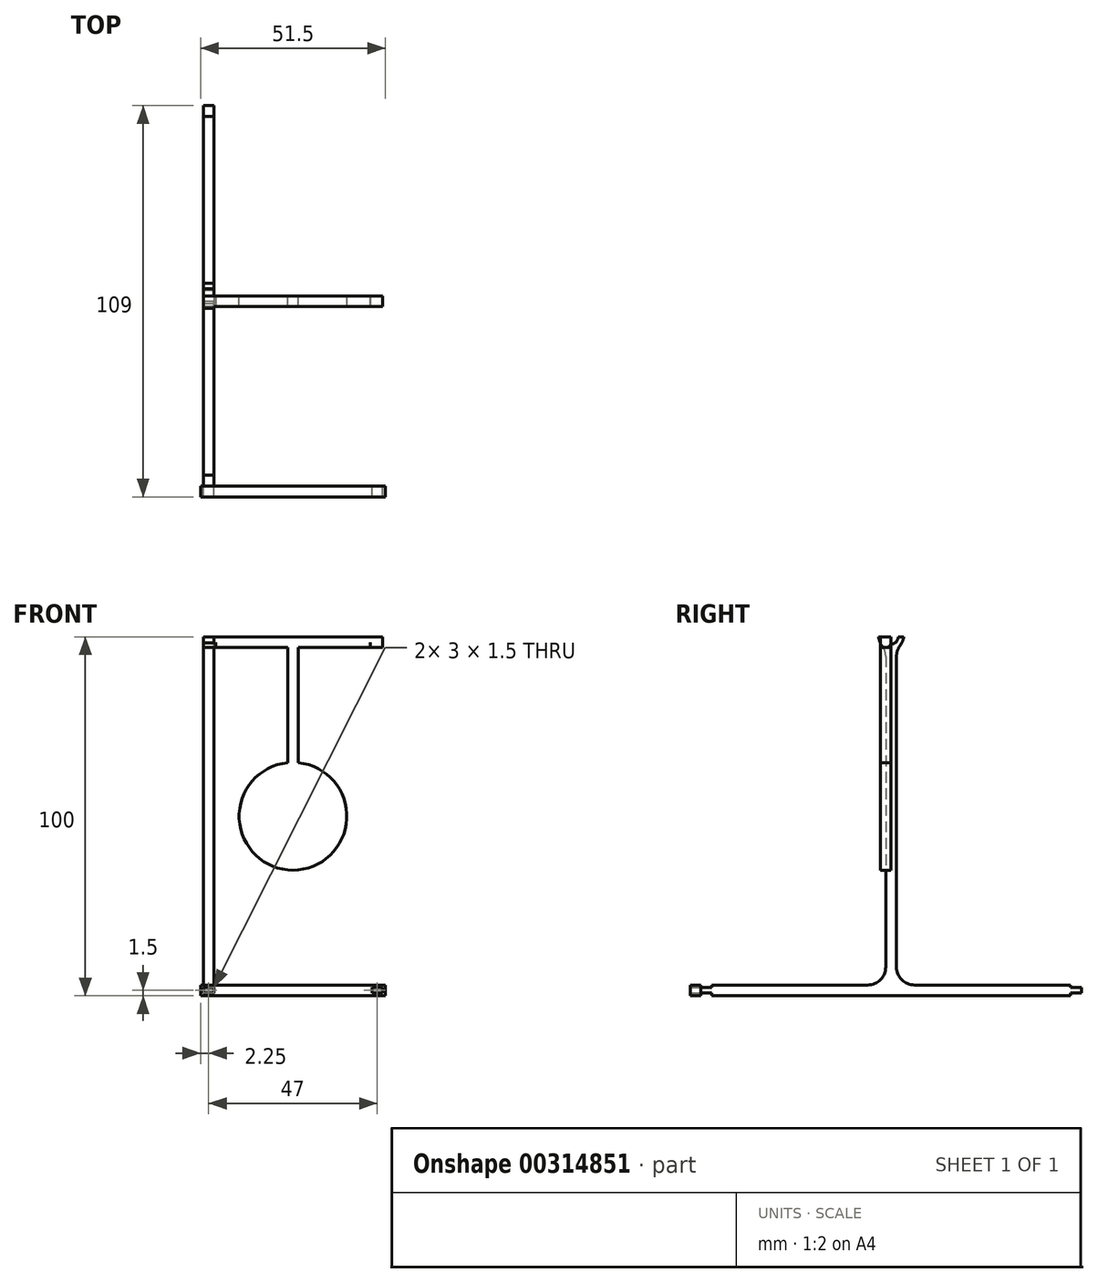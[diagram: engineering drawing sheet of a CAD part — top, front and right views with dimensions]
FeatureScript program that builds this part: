
annotation { "Feature Type Name" : "Feature", "Feature Type Description" : "" }
export const myFeature = defineFeature(function(context is Context, id is Id, definition is map)
    precondition{}
    {
        {
            var Q0;
            Q0=qCreatedBy(makeId("Right.planeOp"),FACE);
            var sketch = newSketch(context, id + "F0", { "sketchPlane" : qUnion([Q0])});
            skLineSegment(sketch, "E0", {"start": v(-2, 100) * mm, "end": v(-3.5, 100) * mm});
            skLineSegment(sketch, "E1", {"start": v(-3.5, 100) * mm, "end": v(-3.5, 98.5) * mm});
            skLineSegment(sketch, "E2", {"start": v(-50, 3) * mm, "end": v(-50, 2.25) * mm});
            skLineSegment(sketch, "E3", {"start": v(-50, 2.25) * mm, "end": v(-53, 2.25) * mm});
            skLineSegment(sketch, "E4", {"start": v(-53, 2.25) * mm, "end": v(-53, 0.75) * mm});
            skLineSegment(sketch, "E5", {"start": v(-53, 0.75) * mm, "end": v(-50, 0.75) * mm});
            skLineSegment(sketch, "E6", {"start": v(-50, 0.75) * mm, "end": v(-50, 0) * mm});
            skLineSegment(sketch, "E7", {"start": v(-50, 0) * mm, "end": v(0, 0) * mm});
            skArc(sketch, "E8", {"start": v(-2, 100) * mm, "mid": v(-1.41, 98.59) * mm, "end": v(0, 98) * mm});
            skPoint(sketch, "E8.third.point", {"position": v(0, 102) * mm});
            skPoint(sketch, "E9.start.orphan", {"position": v(0, 98) * mm});
            skLineSegment(sketch, "E10", {"start": v(-3.5, 98.5) * mm, "end": v(-1.5, 96.5) * mm});
            skLineSegment(sketch, "E11", {"start": v(-1.5, 96.5) * mm, "end": v(-1.5, 3) * mm});
            skLineSegment(sketch, "E12", {"start": v(-50, 3) * mm, "end": v(-1.5, 3) * mm});
            skLineSegment(sketch, "E13.MirrorCS", {"start": v(2, 100) * mm, "end": v(3.5, 100) * mm});
            skLineSegment(sketch, "E14.MirrorCS", {"start": v(3.5, 100) * mm, "end": v(3.5, 98.5) * mm});
            skLineSegment(sketch, "E15.MirrorCS", {"start": v(50, 3) * mm, "end": v(50, 2.25) * mm});
            skLineSegment(sketch, "E16.MirrorCS", {"start": v(50, 2.25) * mm, "end": v(53, 2.25) * mm});
            skLineSegment(sketch, "E17.MirrorCS", {"start": v(53, 2.25) * mm, "end": v(53, 0.75) * mm});
            skLineSegment(sketch, "E18.MirrorCS", {"start": v(53, 0.75) * mm, "end": v(50, 0.75) * mm});
            skLineSegment(sketch, "E19.MirrorCS", {"start": v(50, 0.75) * mm, "end": v(50, 0) * mm});
            skArc(sketch, "E20.MirrorCS", {"start": v(2, 100) * mm, "mid": v(1.41, 98.59) * mm, "end": v(0, 98) * mm});
            skLineSegment(sketch, "E21.MirrorCS", {"start": v(3.5, 98.5) * mm, "end": v(1.5, 96.5) * mm});
            skLineSegment(sketch, "E22.MirrorCS", {"start": v(50, 0) * mm, "end": v(0, 0) * mm});
            skLineSegment(sketch, "E23.MirrorCS", {"start": v(1.5, 96.5) * mm, "end": v(1.5, 3) * mm});
            skLineSegment(sketch, "E24.MirrorCS", {"start": v(50, 3) * mm, "end": v(1.5, 3) * mm});
            skSolve(sketch);
        }
        {
            var Q0;
            Q0=makeQuery(id+"F0.imprint","IMPRINT",FACE,{"disambiguationData":[TD([[makeQuery(id+"F0.imprint","IMPRINT",EDGE,{"derivedFrom":sQuery(id+"F0.wireOp",EDGE,"E0")}),1.0]])]});
            extrude(context, id + "F1", {"entities" : qUnion([Q0]), "depth" : 3 * mm});
        }
        {
            var Q0;
            Q0=makeQuery(id+"F1.opExtrude","SWEPT_EDGE",EDGE,{"disambiguationData":[OSD([sQuery(id+"F0.wireOp",EDGE,"E11"),sQuery(id+"F0.wireOp",EDGE,"E12")])]});
            var Q1;
            Q1=makeQuery(id+"F1.opExtrude","SWEPT_EDGE",EDGE,{"disambiguationData":[OSD([sQuery(id+"F0.wireOp",EDGE,"E23.MirrorCS"),sQuery(id+"F0.wireOp",EDGE,"E24.MirrorCS")])]});
            var Q2;
            Q2=makeQuery(id+"F1.opExtrude","SWEPT_EDGE",EDGE,{"disambiguationData":[OSD([sQuery(id+"F0.wireOp",EDGE,"E14.MirrorCS"),sQuery(id+"F0.wireOp",EDGE,"E21.MirrorCS")])]});
            var Q3;
            Q3=makeQuery(id+"F1.opExtrude","SWEPT_EDGE",EDGE,{"disambiguationData":[OSD([sQuery(id+"F0.wireOp",EDGE,"E1"),sQuery(id+"F0.wireOp",EDGE,"E10")])]});
            fillet(context, id + "F2", {"entities" : qUnion([Q0, Q1, Q2, Q3]), "radius" : 5 * mm, "tangentPropagation" : true, "allowEdgeOverflow" : false});
        }
        {
            var Q0;
            Q0=makeQuery(id+"F1.opExtrude","SWEPT_EDGE",EDGE,{"disambiguationData":[OSD([sQuery(id+"F0.wireOp",EDGE,"E10"),sQuery(id+"F0.wireOp",EDGE,"E11")])]});
            var Q1;
            Q1=makeQuery(id+"F1.opExtrude","SWEPT_EDGE",EDGE,{"disambiguationData":[OSD([sQuery(id+"F0.wireOp",EDGE,"E21.MirrorCS"),sQuery(id+"F0.wireOp",EDGE,"E23.MirrorCS")])]});
            fillet(context, id + "F3", {"entities" : qUnion([Q0, Q1]), "radius" : 5 * mm, "tangentPropagation" : true, "allowEdgeOverflow" : false});
        }
        {
            var Q0;
            Q0=makeQuery(id+"F1.opExtrude","SWEPT_FACE",FACE,{"disambiguationData":[OSD([sQuery(id+"F0.wireOp",EDGE,"E4")])]});
            var sketch = newSketch(context, id + "F4", { "sketchPlane" : qUnion([Q0])});
            skLineSegment(sketch, "E25.bottom", {"start": v(0, 2.25) * mm, "end": v(3, 2.25) * mm});
            skLineSegment(sketch, "E25.top", {"start": v(0, 0.75) * mm, "end": v(3, 0.75) * mm});
            skLineSegment(sketch, "E25.left", {"start": v(0, 2.25) * mm, "end": v(0, 0.75) * mm});
            skLineSegment(sketch, "E25.right", {"start": v(3, 2.25) * mm, "end": v(3, 0.75) * mm});
            skLineSegment(sketch, "E26", {"start": v(0, 0) * mm, "end": v(25, 0) * mm});
            skLineSegment(sketch, "E27.0.3", {"start": v(3, 3) * mm, "end": v(0, 3) * mm});
            skLineSegment(sketch, "E28", {"start": v(0, 3) * mm, "end": v(-0.75, 3) * mm});
            skLineSegment(sketch, "E29", {"start": v(-0.75, 3) * mm, "end": v(-0.75, 0) * mm});
            skLineSegment(sketch, "E30", {"start": v(-0.75, 0) * mm, "end": v(0, 0) * mm});
            skLineSegment(sketch, "E31", {"start": v(3, 3) * mm, "end": v(25, 3) * mm});
            skLineSegment(sketch, "E32", {"start": v(25, 3) * mm, "end": v(25, 0) * mm, "construction": true});
            skLineSegment(sketch, "E33", {"start": v(0, 3) * mm, "end": v(0, 2.25) * mm, "construction": true});
            skLineSegment(sketch, "E34", {"start": v(0, 2.25) * mm, "end": v(-0.75, 2.25) * mm, "construction": true});
            skLineSegment(sketch, "E35.MirrorCS", {"start": v(50, 3) * mm, "end": v(50, 2.25) * mm, "construction": true});
            skLineSegment(sketch, "E36.MirrorCS", {"start": v(50, 3) * mm, "end": v(50.75, 3) * mm});
            skLineSegment(sketch, "E37.MirrorCS", {"start": v(50.75, 0) * mm, "end": v(50, 0) * mm});
            skLineSegment(sketch, "E38.MirrorCS", {"start": v(50, 2.25) * mm, "end": v(50.75, 2.25) * mm, "construction": true});
            skLineSegment(sketch, "E39.MirrorCS", {"start": v(50, 2.25) * mm, "end": v(47, 2.25) * mm});
            skLineSegment(sketch, "E40.MirrorCS", {"start": v(50, 2.25) * mm, "end": v(50, 0.75) * mm});
            skLineSegment(sketch, "E41.MirrorCS", {"start": v(47, 2.25) * mm, "end": v(47, 0.75) * mm});
            skLineSegment(sketch, "E42.MirrorCS", {"start": v(47, 3) * mm, "end": v(50, 3) * mm});
            skLineSegment(sketch, "E43.MirrorCS", {"start": v(47, 3) * mm, "end": v(25, 3) * mm});
            skLineSegment(sketch, "E44.MirrorCS", {"start": v(50, 0) * mm, "end": v(25, 0) * mm});
            skLineSegment(sketch, "E45.MirrorCS", {"start": v(50.75, 3) * mm, "end": v(50.75, 0) * mm});
            skLineSegment(sketch, "E46.MirrorCS", {"start": v(50, 0.75) * mm, "end": v(47, 0.75) * mm});
            skSolve(sketch);
        }
        {
            var Q0;
            Q0=makeQuery(id+"F4.imprint","IMPRINT",FACE,{"disambiguationData":[TD([[makeQuery(id+"F4.imprint","IMPRINT",EDGE,{"derivedFrom":sQuery(id+"F4.wireOp",EDGE,"E25.top")}),1.0]])]});
            extrude(context, id + "F5", {"entities" : qUnion([Q0]), "depth" : 3 * mm});
        }
        {
            var Q0;
            Q0=qCreatedBy(makeId("Front.planeOp"),FACE);
            var sketch = newSketch(context, id + "F6", { "sketchPlane" : qUnion([Q0])});
            skLineSegment(sketch, "E47", {"start": v(26.5, 100) * mm, "end": v(0, 100) * mm});
            skLineSegment(sketch, "E48", {"start": v(0, 100) * mm, "end": v(0, 97) * mm});
            skLineSegment(sketch, "E49", {"start": v(0, 97) * mm, "end": v(23.5, 97) * mm});
            skLineSegment(sketch, "E50", {"start": v(23.5, 97) * mm, "end": v(23.5, 64.92) * mm});
            skArc(sketch, "E51", {"start": v(23.5, 64.92) * mm, "mid": v(10.02, 49.25) * mm, "end": v(25, 35) * mm});
            skPoint(sketch, "E51.centerSnap0", {"position": v(25, 64.92) * mm});
            skLineSegment(sketch, "E52", {"start": v(25, 64.92) * mm, "end": v(25, 100) * mm});
            skLineSegment(sketch, "E53", {"start": v(25, 64.92) * mm, "end": v(25, 35) * mm});
            skPoint(sketch, "E54.start.orphan", {"position": v(26.5, 64.92) * mm});
            skSolve(sketch);
        }
        {
            var Q0;
            {var subQ0=sQuery(id+"F6.wireOp",EDGE,"E48");Q0=makeQuery(id+"F6.imprint","IMPRINT",FACE,{"disambiguationData":[TD([[makeQuery(id+"F6.imprint","IMPRINT",EDGE,{"derivedFrom":subQ0}),1.0]])]});}
            extrude(context, id + "F7", {"entities" : qUnion([Q0]), "depth" : 3 * mm});
        }
        {
            var Q0;
            Q0=makeQuery(id+"F7.opExtrude","SWEPT_FACE",FACE,{"disambiguationData":[OSD([sQuery(id+"F6.wireOp",EDGE,"E48")])]});
            var sketch = newSketch(context, id + "F8", { "sketchPlane" : qUnion([Q0])});
            skArc(sketch, "E55", {"start": v(3, 98.5) * mm, "mid": v(1.5, 97) * mm, "end": v(0, 98.5) * mm});
            skPoint(sketch, "E55.centerSnap0", {"position": v(1.5, 97) * mm});
            skPoint(sketch, "E55.centerSnap1", {"position": v(0, 98.5) * mm});
            skLineSegment(sketch, "E56", {"start": v(0, 98.5) * mm, "end": v(0, 97) * mm});
            skLineSegment(sketch, "E57", {"start": v(0, 97) * mm, "end": v(3, 97) * mm});
            skLineSegment(sketch, "E58", {"start": v(3, 97) * mm, "end": v(3, 98.5) * mm});
            skSolve(sketch);
        }
        {
            var Q0;
            {var subQ0=sQuery(id+"F8.wireOp",EDGE,"E58");Q0=makeQuery(id+"F8.imprint","IMPRINT",FACE,{"disambiguationData":[TD([[makeQuery(id+"F8.imprint","IMPRINT",EDGE,{"derivedFrom":subQ0}),-1.0]])]});}
            var Q1;
            {var subQ0=sQuery(id+"F8.wireOp",EDGE,"E56");Q1=makeQuery(id+"F8.imprint","IMPRINT",FACE,{"disambiguationData":[TD([[makeQuery(id+"F8.imprint","IMPRINT",EDGE,{"derivedFrom":subQ0}),1.0]])]});}
            extrude(context, id + "F9", {"entities" : qUnion([Q0, Q1]), "operationType" : NewBodyOperationType.REMOVE, "oppositeDirection" : true, "depth" : 3.5 * mm});
        }
        {
            var Q0;
            Q0=makeQuery(id+"F7.opExtrude","SWEPT_BODY",BODY,{"disambiguationData":[OSD([sQuery(id+"F6.wireOp",EDGE,"E47"),sQuery(id+"F6.wireOp",EDGE,"E48"),sQuery(id+"F6.wireOp",EDGE,"E49"),sQuery(id+"F6.wireOp",EDGE,"E50"),sQuery(id+"F6.wireOp",EDGE,"E51"),sQuery(id+"F6.wireOp",EDGE,"E52"),sQuery(id+"F6.wireOp",EDGE,"E53")])]});
            var Q1;
            Q1=makeQuery(id+"F7.opExtrude","SWEPT_FACE",FACE,{"disambiguationData":[OSD([sQuery(id+"F6.wireOp",EDGE,"E52"),sQuery(id+"F6.wireOp",EDGE,"E53")])]});
            mirror(context, id + "F10", {"operationType" : NewBodyOperationType.ADD, "entities" : qUnion([Q0]), "mirrorPlane" : qUnion([Q1])});
        }
    });
